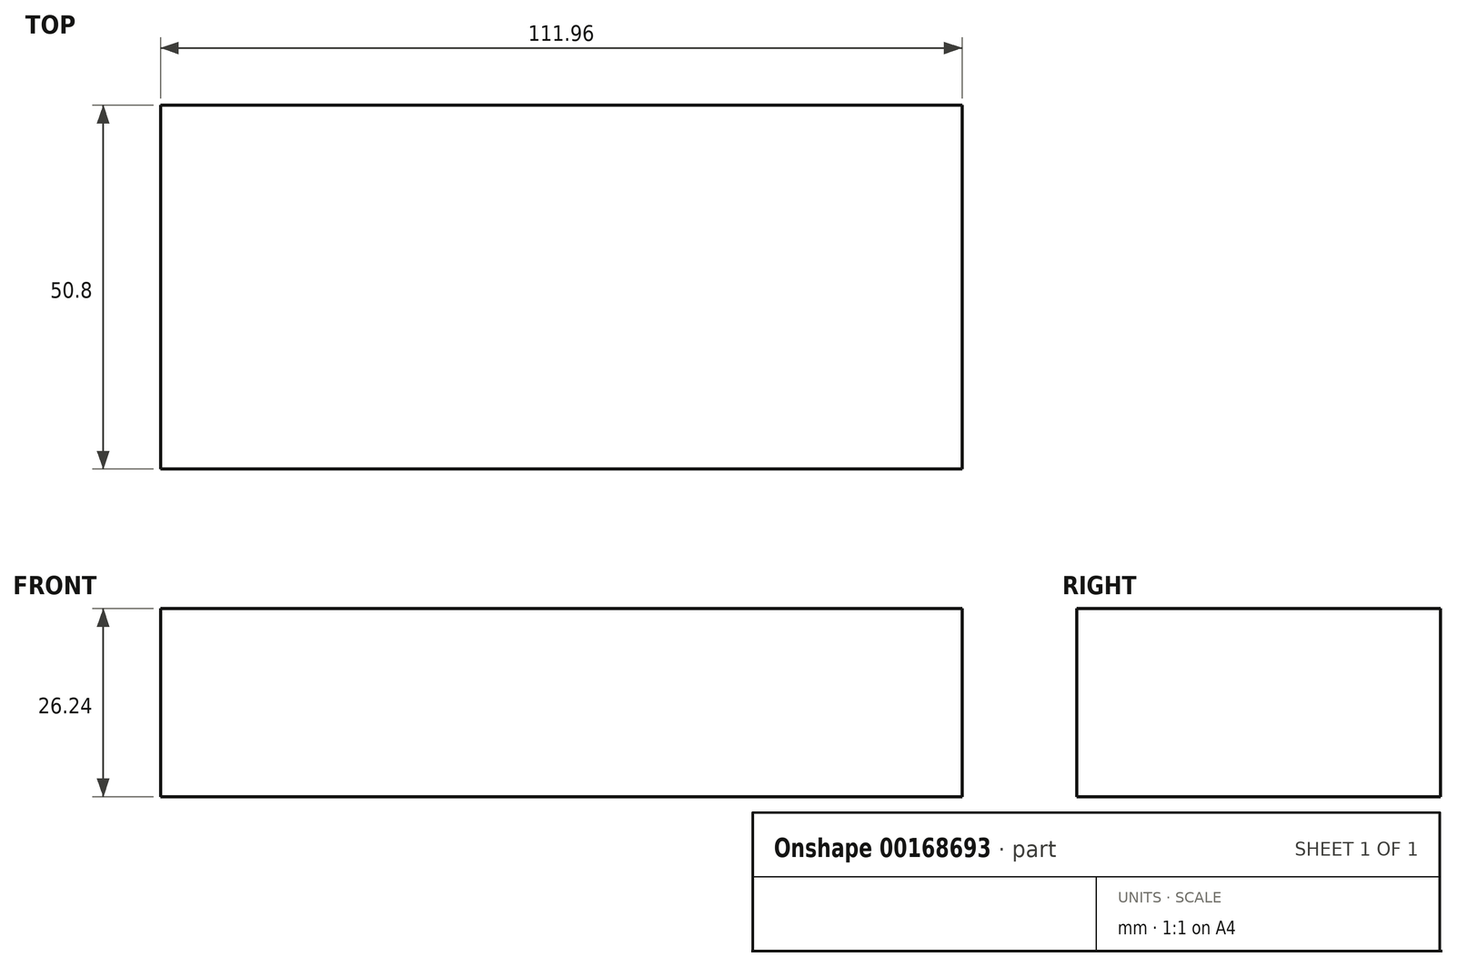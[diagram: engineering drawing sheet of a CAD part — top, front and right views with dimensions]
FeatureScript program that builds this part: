
annotation { "Feature Type Name" : "Feature", "Feature Type Description" : "" }
export const myFeature = defineFeature(function(context is Context, id is Id, definition is map)
    precondition{}
    {
        {
            var Q0;
            Q0=qCreatedBy(makeId("Front.planeOp"),FACE);
            var sketch = newSketch(context, id + "F0", { "sketchPlane" : qUnion([Q0])});
            skLineSegment(sketch, "E0.bottom", {"start": v(55.98, -13.12) * mm, "end": v(-55.98, -13.12) * mm});
            skLineSegment(sketch, "E0.top", {"start": v(55.98, 13.12) * mm, "end": v(-55.98, 13.12) * mm});
            skLineSegment(sketch, "E0.left", {"start": v(55.98, -13.12) * mm, "end": v(55.98, 13.12) * mm});
            skLineSegment(sketch, "E0.right", {"start": v(-55.98, -13.12) * mm, "end": v(-55.98, 13.12) * mm});
            skPoint(sketch, "E0.middle", {"position": v(0, 0) * mm});
            skSolve(sketch);
        }
        {
            var Q0;
            Q0=makeQuery(id+"F0.imprint","IMPRINT",FACE,{"disambiguationData":[TD([[makeQuery(id+"F0.imprint","IMPRINT",EDGE,{"derivedFrom":sQuery(id+"F0.wireOp",EDGE,"E0.bottom")}),-1.0]])]});
            extrude(context, id + "F1", {"entities" : qUnion([Q0]), "depth" : 50.8 * mm});
        }
    });
